# Revit family: IS_ConnectBlue_B9931_BIM_FR
name_source: partatom
category: Plumbing Fixtures
revit_build: Autodesk Revit 2017 (Build: 20160225_1515(x64)
units: mm (PartAtom-declared; Revit-internal decimal feet)

## family parameters
Cut with Voids When Loaded = No
Host = Face
OmniClass Number = 23.45.55.17
OmniClass Title = Mixing Faucets
Part Type = Normal
Room Calculation Point = No
Round Connector Dimension = Use Diameter
Shared = Yes

## types (1)
- B9931AA - CONNECT BLUE SNK MXR R-MTD CHR CAST SPT
    Accessoires = www.idealstandard.be
    Assembly Code = C1030200
    Bim-NomDuProjet = ISI_IdealStandard_ConnectBlue_B9931
    CWFU = 0
    Caractéristiques = Mitigeur Évier Monotrou
    ConseilsDInstallation = www.idealstandard.be
    Cost = 0 $
    CoûtDeRemplacement = 0
    DateDeCréation = 2018_08_15
    Default Elevation = 0 mm  [stored 0 ft]
    Description = Mitigeur Évier Monotrou
    Dimensions = 184 x 57 x 273 mm
    Espace = Interne
    Forme = Complexe
    HWFU = 0
    Hauteur = 184 mm  [stored 0.603675 ft]
    InformationsProduit = www.idealstandard.be
    Largeur = 57 mm  [stored 0.187008 ft]
    LienUtile = www.idealstandard.be
    Longueur = 273 mm  [stored 0.895669 ft]
    Manufacturer = www.idealstandard.be
    Marque = Ideal Standard
    Model = B9931GN
    NBSDescription = Shower heads
    NBSReference = 45-35-70/333
    PoidsNet = 0
    Profondeur = 0 mm  [stored 0 ft]
    Raccordement = Plomberie
    Révision = 1
    URL = www.idealstandard.be
    Uniclass2015Code = Pr_40_20_87_76
    Uniclass2015Title = Shower heads
    UnitéDeMesure = Millimètres
    UnitéDeTemps = An
    UnitéMonétaire = €
    UrlDuFabricant = www.idealstandard.be
    WFU = 0

note: [stored X ft] marks values corroborated as IEEE doubles in the binary element streams (Revit-internal decimal feet)

## geometry (parser evidence)
native form markers: Sweep x2
no freeform markers — native parametric forms only
